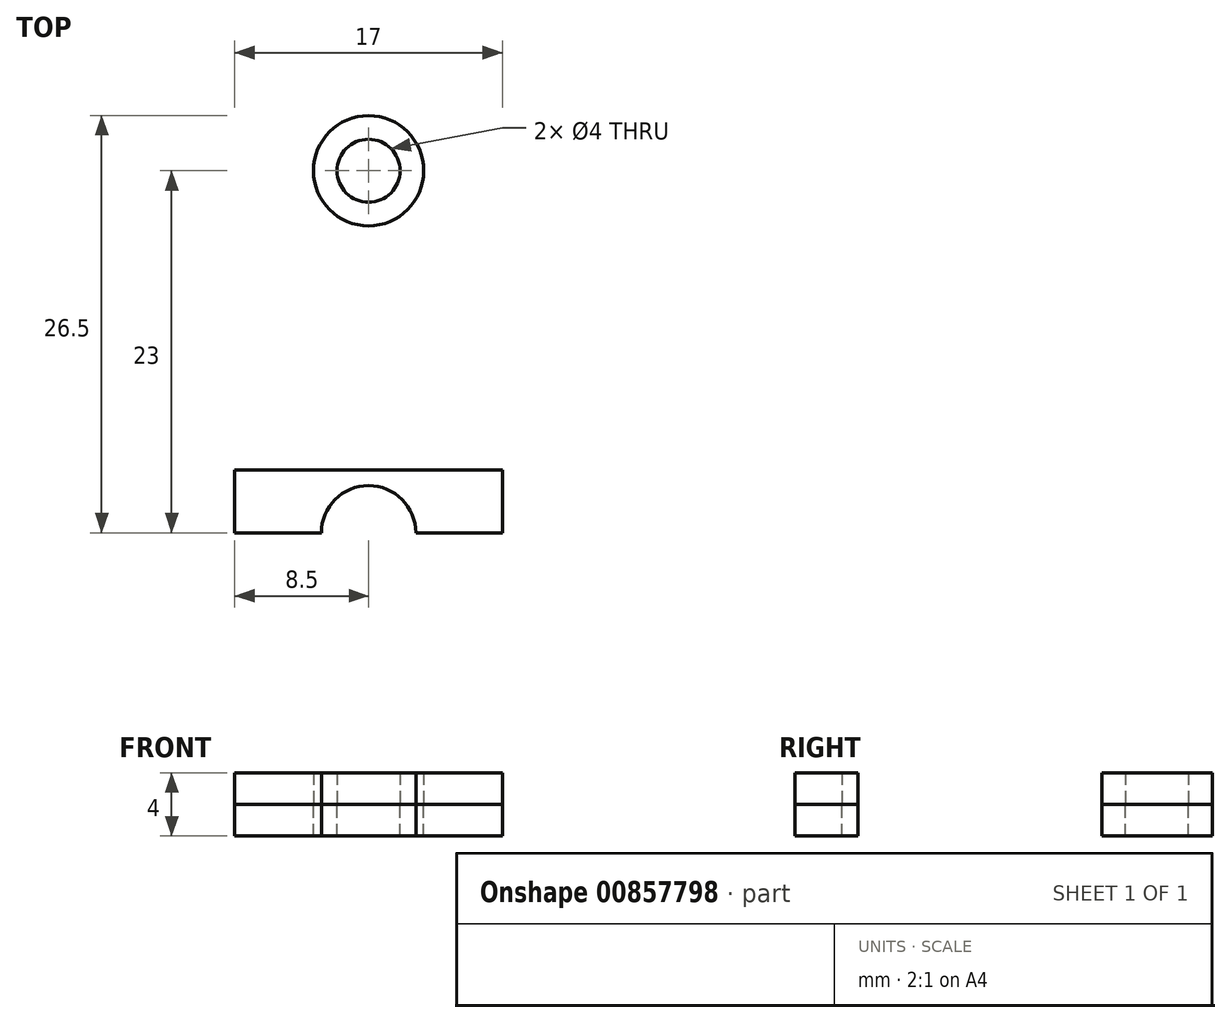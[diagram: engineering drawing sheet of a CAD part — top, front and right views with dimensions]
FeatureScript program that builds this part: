
annotation { "Feature Type Name" : "Feature", "Feature Type Description" : "" }
export const myFeature = defineFeature(function(context is Context, id is Id, definition is map)
    precondition{}
    {
        {
            var Q0;
            Q0=qCreatedBy(makeId("Top.planeOp"),FACE);
            var sketch = newSketch(context, id + "F0", { "sketchPlane" : qUnion([Q0])});
            skLineSegment(sketch, "E0", {"start": v(0, 11.5) * mm, "end": v(0, -11.5) * mm, "construction": true});
            skCircle(sketch, "E1", {"center": v(0, 11.5) * mm, "radius": 2 * mm});
            skArc(sketch, "E2", {"start": v(3, -11.5) * mm, "mid": v(0, -8.5) * mm, "end": v(-3, -11.5) * mm});
            skLineSegment(sketch, "E3", {"start": v(-4.5, -11.5) * mm, "end": v(-8.5, -11.5) * mm});
            skLineSegment(sketch, "E4", {"start": v(4.5, -11.5) * mm, "end": v(8.5, -11.5) * mm});
            skLineSegment(sketch, "E5", {"start": v(-8.5, -11.5) * mm, "end": v(-8.5, -7.5) * mm});
            skLineSegment(sketch, "E6", {"start": v(-4.5, -11.5) * mm, "end": v(-3, -11.5) * mm});
            skLineSegment(sketch, "E7.trimOffspring", {"start": v(3, -11.5) * mm, "end": v(4.5, -11.5) * mm});
            skLineSegment(sketch, "E8", {"start": v(-2, 11.5) * mm, "end": v(-2, -17.52) * mm, "construction": true});
            skLineSegment(sketch, "E9", {"start": v(-8.5, -7.5) * mm, "end": v(1.2, -7.5) * mm, "construction": true});
            skFitSpline(sketch, "E10", {"points": [v(-2, 8.63) * mm, v(-8.5, -7.5) * mm], "startDerivative": vector(0, -25.88) * mm, "endDerivative": vector(-19.5, 0) * mm});
            skFitSpline(sketch, "E11.MirrorCS", {"points": [v(2, 8.63) * mm, v(8.5, -7.5) * mm], "startDerivative": vector(0, -25.88) * mm, "endDerivative": vector(19.5, 0) * mm});
            skLineSegment(sketch, "E12.MirrorCS", {"start": v(8.5, -11.5) * mm, "end": v(8.5, -7.5) * mm});
            skLineSegment(sketch, "E13", {"start": v(-8.5, -7.5) * mm, "end": v(8.5, -7.5) * mm});
            skCircle(sketch, "E14", {"center": v(0, 11.5) * mm, "radius": 3.5 * mm});
            skLineSegment(sketch, "E15", {"start": v(5.7, 9) * mm, "end": v(-5.57, 9) * mm, "construction": true});
            skSolve(sketch);
        }
        {
            var Q0;
            Q0=sQuery(id+"F0.wireOp",EDGE,"E15");
            cPlane(context, id + "F1", {"entities" : qUnion([Q0]), "cplaneType" : CPlaneType.LINE_ANGLE, "offset" : 25 * mm, "angle" : 0 * degree, "width" : 150 * mm, "height" : 150 * mm});
        }
        {
            var Q0;
            Q0=makeQuery(id+"F0.imprint","IMPRINT",FACE,{"disambiguationData":[TD([[makeQuery(id+"F0.imprint","IMPRINT",EDGE,{"derivedFrom":sQuery(id+"F0.wireOp",EDGE,"E1")}),-1.0]])]});
            var Q1;
            Q1=makeQuery(id+"F0.imprint","IMPRINT",FACE,{"disambiguationData":[TD([[makeQuery(id+"F0.imprint","IMPRINT",EDGE,{"derivedFrom":sQuery(id+"F0.wireOp",EDGE,"E2")}),-1.0]])]});
            extrude(context, id + "F2", {"entities" : qUnion([Q0, Q1]), "depth" : 2 * mm, "offsetDistance" : 25 * mm});
        }
        {
            var Q0;
            Q0=makeQuery(id+"F2.opExtrude","CAP_FACE",FACE,{"disambiguationData":[OSD([sQuery(id+"F0.wireOp",EDGE,"E1"),sQuery(id+"F0.wireOp",EDGE,"E2"),sQuery(id+"F0.wireOp",EDGE,"E3"),sQuery(id+"F0.wireOp",EDGE,"E4"),sQuery(id+"F0.wireOp",EDGE,"E5"),sQuery(id+"F0.wireOp",EDGE,"E6"),sQuery(id+"F0.wireOp",EDGE,"E7.trimOffspring"),sQuery(id+"F0.wireOp",EDGE,"E10"),sQuery(id+"F0.wireOp",EDGE,"E11.MirrorCS"),sQuery(id+"F0.wireOp",EDGE,"E12.MirrorCS"),sQuery(id+"F0.wireOp",EDGE,"aEQbBj8d-6Gct-pY18-32jC-V7RseD2QgONP")])],"isStart":false});
            var sketch = newSketch(context, id + "F3", { "sketchPlane" : qUnion([Q0])});
            skCircle(sketch, "E16", {"center": v(0, 11.5) * mm, "radius": 3.5 * mm});
            skCircle(sketch, "E17", {"center": v(0, -11.5) * mm, "radius": 3 * mm});
            skLineSegment(sketch, "E18", {"start": v(0, -11.5) * mm, "end": v(0, -1.5) * mm, "construction": true});
            skLineSegment(sketch, "E19", {"start": v(-7, -1.5) * mm, "end": v(7, -1.5) * mm, "construction": true});
            skSolve(sketch);
        }
        {
            var Q0;
            Q0=sQuery(id+"F3.wireOp",EDGE,"E19");
            cPlane(context, id + "F4", {"entities" : qUnion([Q0]), "cplaneType" : CPlaneType.LINE_ANGLE, "offset" : 25 * mm, "angle" : 0 * degree, "width" : 150 * mm, "height" : 150 * mm});
        }
        {
            var Q0;
            Q0=makeQuery(id+"F2.opExtrude","SWEPT_BODY",BODY,{"disambiguationData":[OSD([sQuery(id+"F0.wireOp",EDGE,"E2"),sQuery(id+"F0.wireOp",EDGE,"E3"),sQuery(id+"F0.wireOp",EDGE,"E4"),sQuery(id+"F0.wireOp",EDGE,"E5"),sQuery(id+"F0.wireOp",EDGE,"E6"),sQuery(id+"F0.wireOp",EDGE,"E7.trimOffspring"),sQuery(id+"F0.wireOp",EDGE,"E12.MirrorCS"),sQuery(id+"F0.wireOp",EDGE,"E13")])]});
            var Q1;
            Q1=makeQuery(id+"F2.opExtrude","SWEPT_BODY",BODY,{"disambiguationData":[OSD([sQuery(id+"F0.wireOp",EDGE,"E1"),sQuery(id+"F0.wireOp",EDGE,"E14")])]});
            var Q2;
            Q2=qCreatedBy(makeId("Top.planeOp"),FACE);
            mirror(context, id + "F5", {"entities" : qUnion([Q0, Q1]), "mirrorPlane" : qUnion([Q2])});
        }
    });
